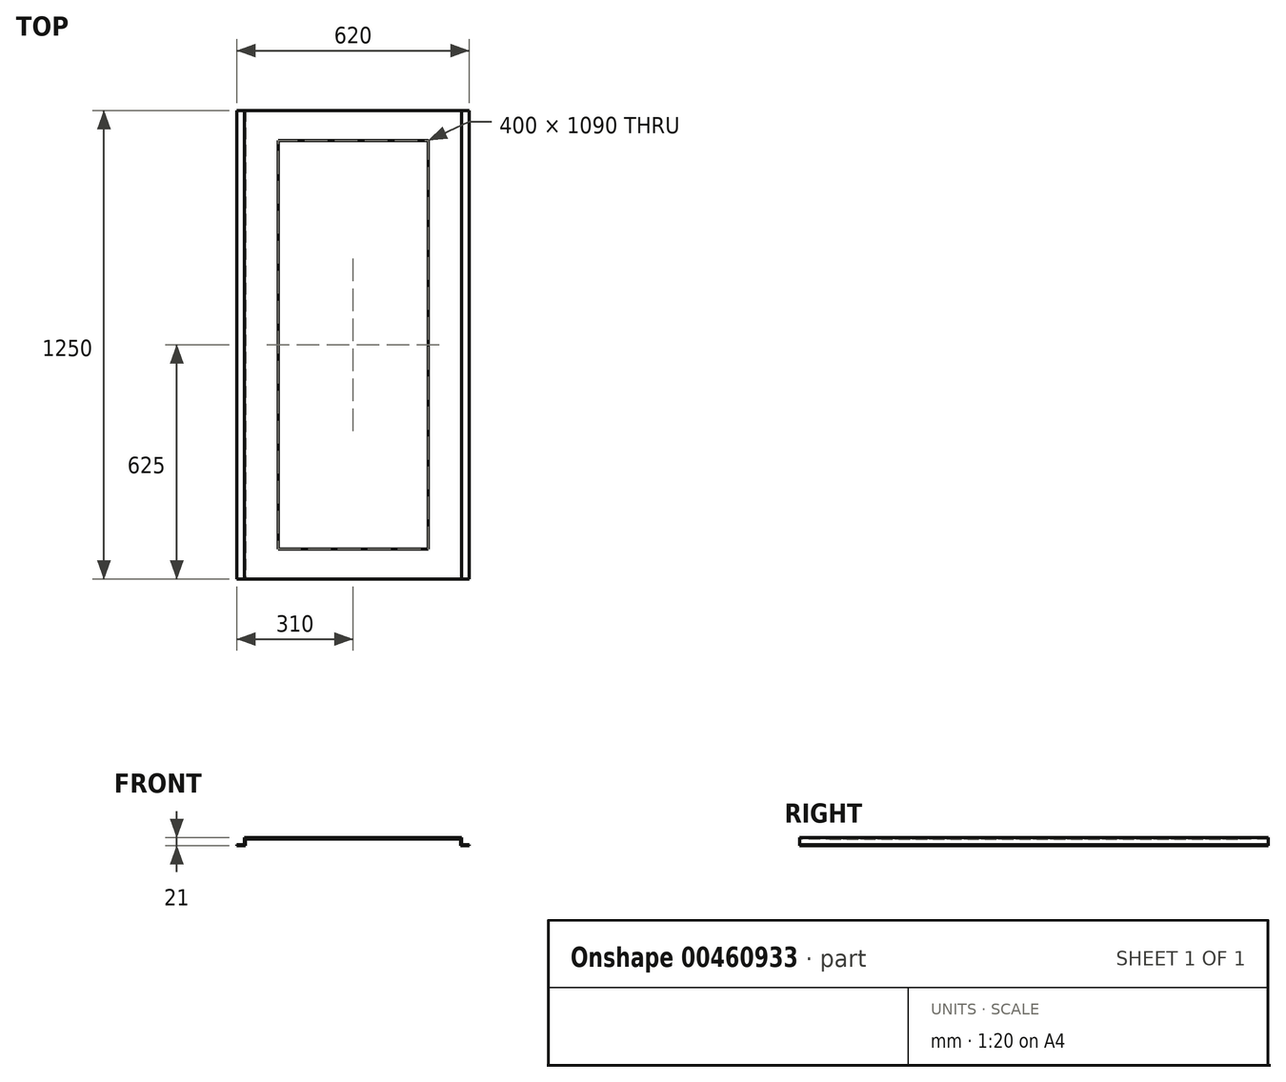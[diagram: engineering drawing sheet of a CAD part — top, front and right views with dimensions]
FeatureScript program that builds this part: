
annotation { "Feature Type Name" : "Feature", "Feature Type Description" : "" }
export const myFeature = defineFeature(function(context is Context, id is Id, definition is map)
    precondition{}
    {
        {
            var Q0;
            Q0=qCreatedBy(makeId("Top.planeOp"),FACE);
            var sketch = newSketch(context, id + "F0", { "sketchPlane" : qUnion([Q0])});
            skLineSegment(sketch, "E0.bottom", {"start": v(-200, -545) * mm, "end": v(200, -545) * mm});
            skLineSegment(sketch, "E0.top", {"start": v(-200, 545) * mm, "end": v(200, 545) * mm});
            skLineSegment(sketch, "E0.left", {"start": v(-200, -545) * mm, "end": v(-200, 545) * mm});
            skLineSegment(sketch, "E0.right", {"start": v(200, -545) * mm, "end": v(200, 545) * mm});
            skPoint(sketch, "E0.middle", {"position": v(0, 0) * mm});
            skLineSegment(sketch, "E1.bottom", {"start": v(-290, -625) * mm, "end": v(290, -625) * mm});
            skLineSegment(sketch, "E1.top", {"start": v(-290, 625) * mm, "end": v(290, 625) * mm});
            skLineSegment(sketch, "E1.left", {"start": v(-290, -625) * mm, "end": v(-290, 625) * mm});
            skLineSegment(sketch, "E1.right", {"start": v(290, -625) * mm, "end": v(290, 625) * mm});
            skSolve(sketch);
        }
        {
            var Q0;
            Q0=makeQuery(id+"F0.imprint","IMPRINT",FACE,{"disambiguationData":[TD([[makeQuery(id+"F0.imprint","IMPRINT",EDGE,{"derivedFrom":sQuery(id+"F0.wireOp",EDGE,"E0.bottom")}),-1.0]])]});
            extrude(context, id + "F1", {"entities" : qUnion([Q0]), "depth" : 3 * mm, "offsetDistance" : 25 * mm});
        }
        {
            var Q0;
            Q0=makeQuery(id+"F1.opExtrude","SWEPT_FACE",FACE,{"disambiguationData":[OSD([sQuery(id+"F0.wireOp",EDGE,"E1.bottom")])]});
            var sketch = newSketch(context, id + "F2", { "sketchPlane" : qUnion([Q0])});
            skLineSegment(sketch, "E2", {"start": v(-290, 0) * mm, "end": v(-290, -15) * mm});
            skLineSegment(sketch, "E3", {"start": v(-290, -15) * mm, "end": v(-310, -15) * mm});
            skLineSegment(sketch, "E4", {"start": v(-310, -15) * mm, "end": v(-310, -18) * mm});
            skLineSegment(sketch, "E5", {"start": v(-310, -18) * mm, "end": v(-287, -18) * mm});
            skLineSegment(sketch, "E6", {"start": v(-287, -18) * mm, "end": v(-287, 0) * mm});
            skLineSegment(sketch, "E7.MirrorCS", {"start": v(290, 0) * mm, "end": v(290, -15) * mm});
            skLineSegment(sketch, "E8.MirrorCS", {"start": v(287, -18) * mm, "end": v(287, 0) * mm});
            skLineSegment(sketch, "E9.MirrorCS", {"start": v(310, -18) * mm, "end": v(287, -18) * mm});
            skLineSegment(sketch, "E10.MirrorCS", {"start": v(290, -15) * mm, "end": v(310, -15) * mm});
            skLineSegment(sketch, "E11.MirrorCS", {"start": v(310, -15) * mm, "end": v(310, -18) * mm});
            skSolve(sketch);
        }
        {
            var Q0;
            {var subQ0=sQuery(id+"F2.wireOp",EDGE,"E2");Q0=makeQuery(id+"F2.imprint","IMPRINT",FACE,{"disambiguationData":[TD([[makeQuery(id+"F2.imprint","IMPRINT",EDGE,{"derivedFrom":subQ0}),1.0]])]});}
            var Q1;
            {var subQ1=sQuery(id+"F2.wireOp",EDGE,"E7.MirrorCS");Q1=makeQuery(id+"F2.imprint","IMPRINT",FACE,{"disambiguationData":[TD([[makeQuery(id+"F2.imprint","IMPRINT",EDGE,{"derivedFrom":subQ1}),-1.0]])]});}
            extrude(context, id + "F3", {"entities" : qUnion([Q0, Q1]), "operationType" : NewBodyOperationType.ADD, "oppositeDirection" : true, "depth" : 1250 * mm, "offsetDistance" : 25 * mm});
        }
    });
